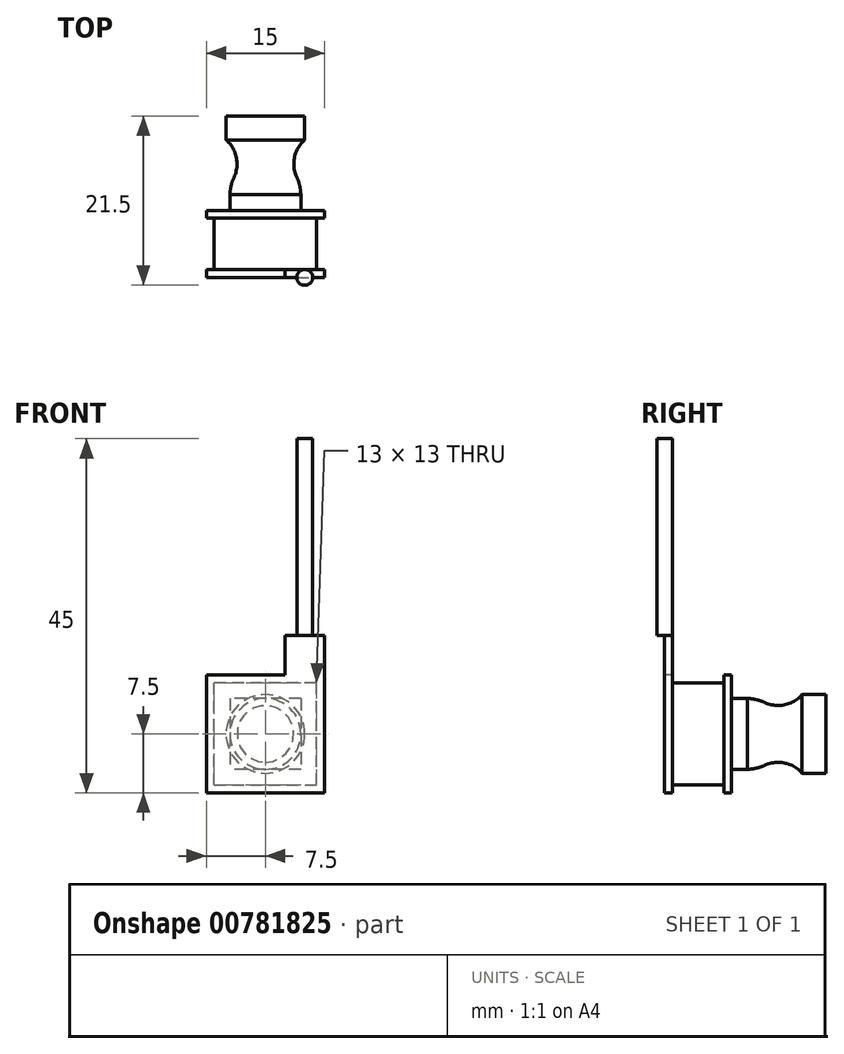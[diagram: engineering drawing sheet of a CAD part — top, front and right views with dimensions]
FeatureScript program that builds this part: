
annotation { "Feature Type Name" : "Feature", "Feature Type Description" : "" }
export const myFeature = defineFeature(function(context is Context, id is Id, definition is map)
    precondition{}
    {
        {
            var Q0;
            Q0=qCreatedBy(makeId("Top.planeOp"),FACE);
            var sketch = newSketch(context, id + "F0", { "sketchPlane" : qUnion([Q0])});
            skLineSegment(sketch, "E0.bottom", {"start": v(-7.5, 0) * mm, "end": v(7.5, 0) * mm});
            skLineSegment(sketch, "E0.top", {"start": v(-7.5, -8.5) * mm, "end": v(7.5, -8.5) * mm});
            skLineSegment(sketch, "E0.left", {"start": v(-7.5, 0) * mm, "end": v(-7.5, -8.5) * mm});
            skLineSegment(sketch, "E0.right", {"start": v(7.5, 0) * mm, "end": v(7.5, -8.5) * mm});
            skPoint(sketch, "E1", {"position": v(0, 0) * mm});
            skSolve(sketch);
        }
        {
            var Q0;
            Q0=makeQuery(id+"F0.imprint","IMPRINT",FACE,{"disambiguationData":[TD([[makeQuery(id+"F0.imprint","IMPRINT",EDGE,{"derivedFrom":sQuery(id+"F0.wireOp",EDGE,"E0.bottom")}),-1.0]])]});
            extrude(context, id + "F1", {"entities" : qUnion([Q0]), "depth" : 15 * mm, "offsetDistance" : 25 * mm});
        }
        {
            var Q0;
            Q0=makeQuery(id+"F1.opExtrude","CAP_FACE",FACE,{"disambiguationData":[OSD([sQuery(id+"F0.wireOp",EDGE,"E0.bottom"),sQuery(id+"F0.wireOp",EDGE,"E0.top"),sQuery(id+"F0.wireOp",EDGE,"E0.left"),sQuery(id+"F0.wireOp",EDGE,"E0.right")])],"isStart":false});
            var sketch = newSketch(context, id + "F2", { "sketchPlane" : qUnion([Q0])});
            skLineSegment(sketch, "E2", {"start": v(-7.5, -7.5) * mm, "end": v(7.5, -7.5) * mm});
            skLineSegment(sketch, "E3", {"start": v(7.5, -1) * mm, "end": v(7.5, -7.5) * mm});
            skLineSegment(sketch, "E4", {"start": v(7.5, -1) * mm, "end": v(-7.5, -1) * mm});
            skLineSegment(sketch, "E5", {"start": v(-7.5, -1) * mm, "end": v(-7.5, -7.5) * mm});
            skSolve(sketch);
        }
        {
            var Q0;
            Q0=makeQuery(id+"F2.imprint","IMPRINT",FACE,{"disambiguationData":[TD([[makeQuery(id+"F2.imprint","IMPRINT",EDGE,{"derivedFrom":sQuery(id+"F2.wireOp",EDGE,"E2")}),1.0]])]});
            extrude(context, id + "F3", {"entities" : qUnion([Q0]), "operationType" : NewBodyOperationType.REMOVE, "oppositeDirection" : true, "depth" : 1 * mm, "offsetDistance" : 25 * mm});
        }
        {
            var Q0;
            Q0=makeQuery(id+"F1.opExtrude","SWEPT_FACE",FACE,{"disambiguationData":[OSD([sQuery(id+"F0.wireOp",EDGE,"E0.right")])]});
            var sketch = newSketch(context, id + "F4", { "sketchPlane" : qUnion([Q0])});
            skLineSegment(sketch, "E6", {"start": v(-1, 14) * mm, "end": v(-1, 0) * mm});
            skLineSegment(sketch, "E7", {"start": v(-7.5, 0) * mm, "end": v(-1, 0) * mm});
            skLineSegment(sketch, "E8", {"start": v(-7.5, 0) * mm, "end": v(-7.5, 14) * mm});
            skLineSegment(sketch, "E9", {"start": v(-1, 14) * mm, "end": v(-7.5, 14) * mm});
            skSolve(sketch);
        }
        {
            var Q0;
            Q0=makeQuery(id+"F4.imprint","IMPRINT",FACE,{"disambiguationData":[TD([[makeQuery(id+"F4.imprint","IMPRINT",EDGE,{"derivedFrom":sQuery(id+"F4.wireOp",EDGE,"E6")}),-1.0]])]});
            extrude(context, id + "F5", {"entities" : qUnion([Q0]), "operationType" : NewBodyOperationType.REMOVE, "oppositeDirection" : true, "depth" : 1 * mm, "offsetDistance" : 25 * mm});
        }
        {
            var Q0;
            Q0=makeQuery(id+"F1.opExtrude","CAP_FACE",FACE,{"disambiguationData":[OSD([sQuery(id+"F0.wireOp",EDGE,"E0.bottom"),sQuery(id+"F0.wireOp",EDGE,"E0.top"),sQuery(id+"F0.wireOp",EDGE,"E0.left"),sQuery(id+"F0.wireOp",EDGE,"E0.right")])],"isStart":true});
            var sketch = newSketch(context, id + "F6", { "sketchPlane" : qUnion([Q0])});
            skLineSegment(sketch, "E10", {"start": v(6.5, 1) * mm, "end": v(-7.5, 1) * mm});
            skPoint(sketch, "E10.endSnap0", {"position": v(-7.5, 4.25) * mm});
            skLineSegment(sketch, "E11", {"start": v(-7.5, 7.5) * mm, "end": v(-7.5, 1) * mm});
            skLineSegment(sketch, "E12", {"start": v(-7.5, 7.5) * mm, "end": v(6.5, 7.5) * mm});
            skLineSegment(sketch, "E13", {"start": v(6.5, 1) * mm, "end": v(6.5, 7.5) * mm});
            skSolve(sketch);
        }
        {
            var Q0;
            Q0=makeQuery(id+"F6.imprint","IMPRINT",FACE,{"disambiguationData":[TD([[makeQuery(id+"F6.imprint","IMPRINT",EDGE,{"derivedFrom":sQuery(id+"F6.wireOp",EDGE,"E10")}),-1.0]])]});
            extrude(context, id + "F7", {"entities" : qUnion([Q0]), "operationType" : NewBodyOperationType.REMOVE, "oppositeDirection" : true, "depth" : 1 * mm, "offsetDistance" : 25 * mm});
        }
        {
            var Q0;
            Q0=makeQuery(id+"F1.opExtrude","SWEPT_FACE",FACE,{"disambiguationData":[OSD([sQuery(id+"F0.wireOp",EDGE,"E0.left")])]});
            var sketch = newSketch(context, id + "F8", { "sketchPlane" : qUnion([Q0])});
            skLineSegment(sketch, "E14", {"start": v(7.5, 1) * mm, "end": v(7.5, 14) * mm});
            skLineSegment(sketch, "E15", {"start": v(7.5, 14) * mm, "end": v(1, 14) * mm});
            skLineSegment(sketch, "E16", {"start": v(1, 14) * mm, "end": v(1, 1) * mm});
            skLineSegment(sketch, "E17", {"start": v(1, 1) * mm, "end": v(7.5, 1) * mm});
            skSolve(sketch);
        }
        {
            var Q0;
            Q0=makeQuery(id+"F8.imprint","IMPRINT",FACE,{"disambiguationData":[TD([[makeQuery(id+"F8.imprint","IMPRINT",EDGE,{"derivedFrom":sQuery(id+"F8.wireOp",EDGE,"E14")}),1.0]])]});
            extrude(context, id + "F9", {"entities" : qUnion([Q0]), "operationType" : NewBodyOperationType.REMOVE, "oppositeDirection" : true, "depth" : 1 * mm, "offsetDistance" : 25 * mm});
        }
        {
            var Q0;
            {var subQ0=sQuery(id+"F0.wireOp",EDGE,"E0.top");var subQ1=sQuery(id+"F0.wireOp",EDGE,"E0.left");var subQ2=sQuery(id+"F0.wireOp",EDGE,"E0.right");Q0=makeQuery(id+"F3.boolean.opBoolean","SPLIT",FACE,{"disambiguationData":[TD([makeQuery(id+"F1.opExtrude","SWEPT_FACE",FACE,{"disambiguationData":[OSD([subQ0])]})])],"derivedFrom":makeQuery(id+"F1.opExtrude","CAP_FACE",FACE,{"disambiguationData":[OSD([sQuery(id+"F0.wireOp",EDGE,"E0.bottom"),subQ0,subQ1,subQ2])],"isStart":false})});}
            var sketch = newSketch(context, id + "F10", { "sketchPlane" : qUnion([Q0])});
            skLineSegment(sketch, "E18.bottom", {"start": v(7.5, -7.5) * mm, "end": v(2.5, -7.5) * mm});
            skLineSegment(sketch, "E18.top", {"start": v(7.5, -8.5) * mm, "end": v(2.5, -8.5) * mm});
            skLineSegment(sketch, "E18.left", {"start": v(7.5, -7.5) * mm, "end": v(7.5, -8.5) * mm});
            skLineSegment(sketch, "E18.right", {"start": v(2.5, -7.5) * mm, "end": v(2.5, -8.5) * mm});
            skSolve(sketch);
        }
        {
            var Q0;
            Q0=makeQuery(id+"F10.imprint","IMPRINT",FACE,{"disambiguationData":[TD([[makeQuery(id+"F10.imprint","IMPRINT",EDGE,{"derivedFrom":sQuery(id+"F10.wireOp",EDGE,"E18.bottom")}),1.0]])]});
            var Q1;
            Q1=makeQuery(id+"F10.imprint","IMPRINT",FACE,{"disambiguationData":[TD([[makeQuery(id+"F10.imprint","IMPRINT",EDGE,{"derivedFrom":sQuery(id+"F10.wireOp",EDGE,"E18.bottom")}),-1.0]])]});
            extrude(context, id + "F11", {"entities" : qUnion([Q0, Q1]), "operationType" : NewBodyOperationType.ADD, "depth" : 5 * mm, "offsetDistance" : 25 * mm});
        }
        {
            var Q0;
            Q0=makeQuery(id+"F1.opExtrude","SWEPT_FACE",FACE,{"disambiguationData":[OSD([sQuery(id+"F0.wireOp",EDGE,"E0.bottom")])]});
            var sketch = newSketch(context, id + "F12", { "sketchPlane" : qUnion([Q0])});
            skLineSegment(sketch, "E19.bottom", {"start": v(-4.5, 12) * mm, "end": v(4.5, 12) * mm});
            skLineSegment(sketch, "E19.left", {"start": v(-4.5, 12) * mm, "end": v(-4.5, 3) * mm});
            skLineSegment(sketch, "E19.right", {"start": v(4.5, 12) * mm, "end": v(4.5, 3) * mm});
            skLineSegment(sketch, "E20", {"start": v(-4.5, 3) * mm, "end": v(4.5, 3) * mm});
            skSolve(sketch);
        }
        {
            var Q0;
            Q0=makeQuery(id+"F12.imprint","IMPRINT",FACE,{"disambiguationData":[TD([[makeQuery(id+"F12.imprint","IMPRINT",EDGE,{"derivedFrom":sQuery(id+"F12.wireOp",EDGE,"E19.bottom")}),-1.0]])]});
            extrude(context, id + "F13", {"entities" : qUnion([Q0]), "operationType" : NewBodyOperationType.ADD, "depth" : 2 * mm, "offsetDistance" : 25 * mm});
        }
        {
            var Q0;
            Q0=qCreatedBy(makeId("Right.planeOp"),FACE);
            var sketch = newSketch(context, id + "F14", { "sketchPlane" : qUnion([Q0])});
            skLineSegment(sketch, "E21.0", {"start": v(2, 12) * mm, "end": v(2, 3) * mm});
            skPoint(sketch, "E22", {"position": v(2, 7.5) * mm});
            skArc(sketch, "E23", {"start": v(4.2, 11.49) * mm, "mid": v(3.12, 11.86) * mm, "end": v(2, 12) * mm});
            skArc(sketch, "E24", {"start": v(4.2, 11.49) * mm, "mid": v(6.75, 11.2) * mm, "end": v(8.97, 12.5) * mm});
            skLineSegment(sketch, "E25", {"start": v(12, 12.5) * mm, "end": v(12, 7.5) * mm});
            skLineSegment(sketch, "E26", {"start": v(2, 7.5) * mm, "end": v(12, 7.5) * mm});
            skLineSegment(sketch, "E27", {"start": v(8.97, 12.5) * mm, "end": v(12, 12.5) * mm});
            skSolve(sketch);
        }
        {
            var Q0;
            {var subQ0=sQuery(id+"F14.wireOp",EDGE,"E23");Q0=makeQuery(id+"F14.imprint","IMPRINT",FACE,{"disambiguationData":[TD([[makeQuery(id+"F14.imprint","IMPRINT",EDGE,{"derivedFrom":subQ0}),1.0]])]});}
            var Q1;
            Q1=sQuery(id+"F14.wireOp",EDGE,"E23");
            var Q2;
            Q2=sQuery(id+"F14.wireOp",EDGE,"E24");
            var Q3;
            Q3=sQuery(id+"F14.wireOp",EDGE,"RN2ExxDk-MmCI-8Q1F-PKpd-Cxy1GEaTXMnH");
            var Q4;
            Q4=sQuery(id+"F14.wireOp",EDGE,"LpgZqQ8T-spVM-kQOA-6sK7-UBdbXxRNCnj0");
            var Q5;
            Q5=sQuery(id+"F14.wireOp",EDGE,"E26");
            revolve(context, id + "F15", {"operationType" : NewBodyOperationType.ADD, "surfaceOperationType" : NewSurfaceOperationType.NEW, "entities" : qUnion([Q0]), "surfaceEntities" : qUnion([Q1, Q2, Q3, Q4]), "axis" : qUnion([Q5]), "revolveType" : RevolveType.FULL});
        }
        {
            var Q0;
            Q0=makeQuery(id+"F11.opExtrude","CAP_FACE",FACE,{"disambiguationData":[OSD([sQuery(id+"F10.wireOp",EDGE,"E18.bottom"),sQuery(id+"F10.wireOp",EDGE,"E18.top"),sQuery(id+"F10.wireOp",EDGE,"E18.left"),sQuery(id+"F10.wireOp",EDGE,"E18.right")])],"isStart":false});
            var sketch = newSketch(context, id + "F16", { "sketchPlane" : qUnion([Q0])});
            skCircle(sketch, "E28", {"center": v(5, -8.5) * mm, "radius": 1 * mm});
            skSolve(sketch);
        }
        {
            var Q0;
            {var subQ0=sQuery(id+"F16.wireOp",EDGE,"E28");var subQ1=makeQuery(id+"F16.imprint","INTERSECT",VERTEX,{"derivedFrom":[makeQuery(id+"F11.opExtrude","CAP_EDGE",EDGE,{"disambiguationData":[OSD([sQuery(id+"F10.wireOp",EDGE,"E18.bottom")])],"isStart":false}),subQ0]});Q0=makeQuery(id+"F16.imprint","IMPRINT",FACE,{"disambiguationData":[TD([[makeQuery(id+"F16.imprint","IMPRINT",EDGE,{"disambiguationData":[TD([[subQ1,1.0]])],"derivedFrom":subQ0}),1.0]])]});}
            var Q1;
            {var subQ0=sQuery(id+"F16.wireOp",EDGE,"E28");var subQ1=makeQuery(id+"F11.opExtrude","CAP_EDGE",EDGE,{"disambiguationData":[OSD([sQuery(id+"F10.wireOp",EDGE,"E18.top")])],"isStart":false});var subQ2=makeQuery(id+"F16.imprint","INTERSECT",VERTEX,{"disambiguationData":[OD(0.0)],"derivedFrom":[subQ1,subQ0]});Q1=makeQuery(id+"F16.imprint","IMPRINT",FACE,{"disambiguationData":[TD([[makeQuery(id+"F16.imprint","IMPRINT",EDGE,{"disambiguationData":[TD([[subQ2,1.0]])],"derivedFrom":subQ0}),1.0]])]});}
            extrude(context, id + "F17", {"entities" : qUnion([Q0, Q1]), "operationType" : NewBodyOperationType.ADD, "depth" : 25 * mm, "offsetDistance" : 25 * mm});
        }
    });
